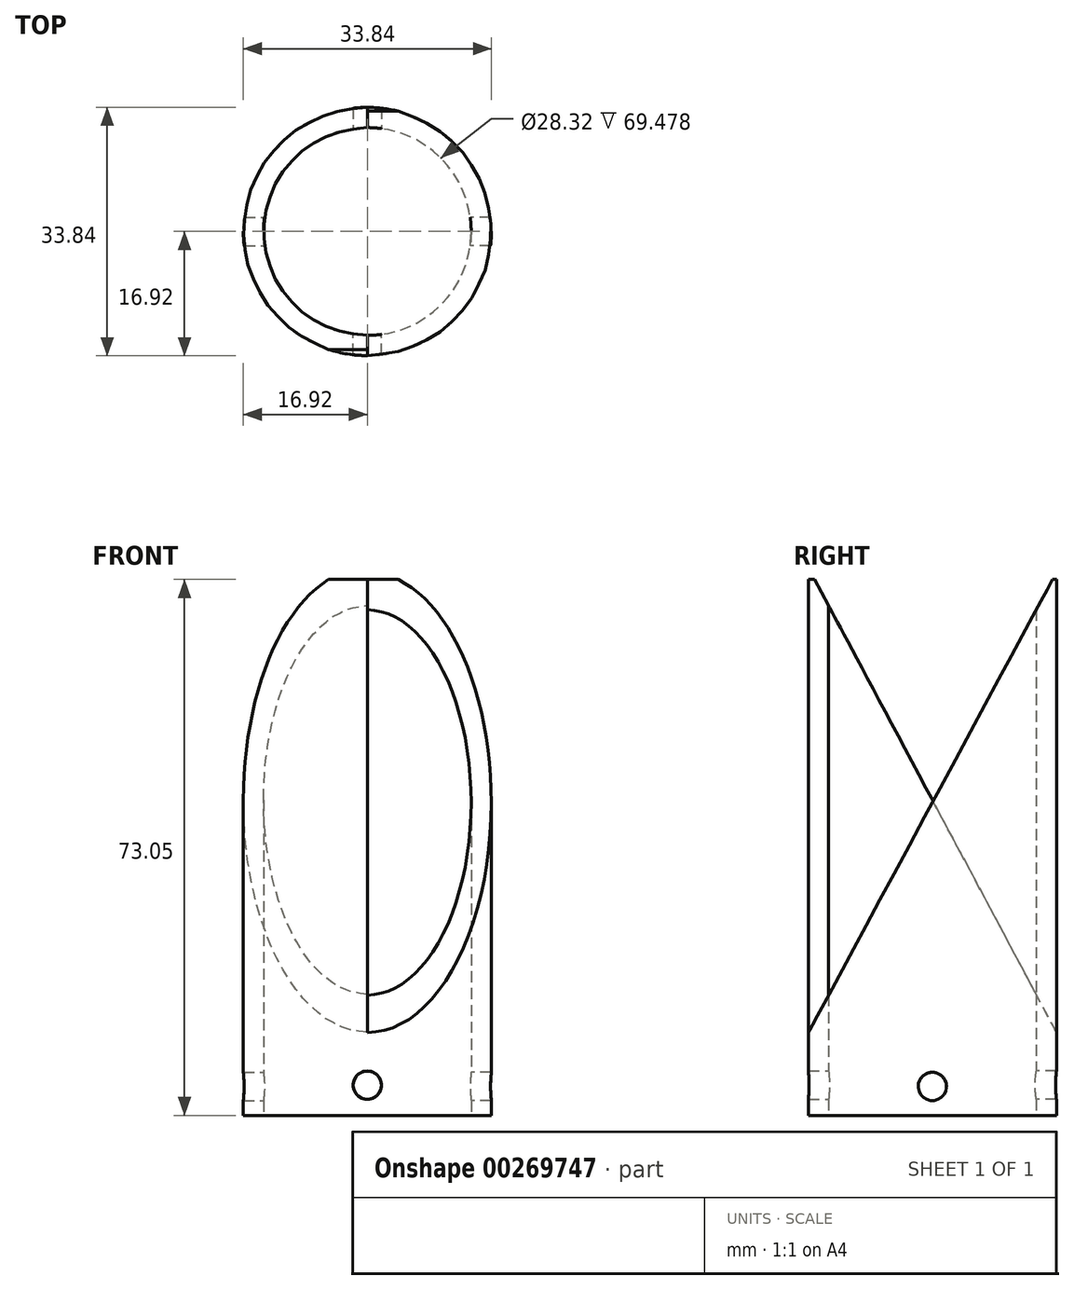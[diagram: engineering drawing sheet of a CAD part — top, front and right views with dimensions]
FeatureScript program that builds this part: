
annotation { "Feature Type Name" : "Feature", "Feature Type Description" : "" }
export const myFeature = defineFeature(function(context is Context, id is Id, definition is map)
    precondition{}
    {
        {
            var Q0;
            Q0=qCreatedBy(makeId("Top.planeOp"),FACE);
            var sketch = newSketch(context, id + "F0", { "sketchPlane" : qUnion([Q0])});
            skCircle(sketch, "E0", {"center": v(0, 0) * mm, "radius": 16.92 * mm});
            skCircle(sketch, "E1", {"center": v(0, 0) * mm, "radius": 14.16 * mm});
            skSolve(sketch);
        }
        {
            var Q0;
            Q0 = qSketchRegion(id + "F0", true);
            extrude(context, id + "F1", {"entities" : qUnion([Q0]), "depth" : 73.05 * mm});
        }
        {
            var Q0;
            Q0=qCreatedBy(makeId("Right.planeOp"),FACE);
            var sketch = newSketch(context, id + "F2", { "sketchPlane" : qUnion([Q0])});
            skLineSegment(sketch, "E2", {"start": v(-18.92, 7.55) * mm, "end": v(19.26, 78.39) * mm});
            skLineSegment(sketch, "E3", {"start": v(19.26, 78.39) * mm, "end": v(-18.28, 78.39) * mm});
            skLineSegment(sketch, "E4", {"start": v(-18.28, 78.39) * mm, "end": v(-18.92, 7.55) * mm});
            skSolve(sketch);
        }
        {
            var Q0;
            Q0 = qSketchRegion(id + "F2", true);
            extrude(context, id + "F3", {"entities" : qUnion([Q0]), "operationType" : NewBodyOperationType.REMOVE, "depth" : 58.42 * mm});
        }
        {
            var Q0;
            Q0=qCreatedBy(makeId("Right.planeOp"),FACE);
            var sketch = newSketch(context, id + "F4", { "sketchPlane" : qUnion([Q0])});
            skLineSegment(sketch, "E5", {"start": v(18.2, 8.96) * mm, "end": v(-19.36, 79.2) * mm});
            skLineSegment(sketch, "E6", {"start": v(-19.36, 79.2) * mm, "end": v(23.54, 79.2) * mm});
            skLineSegment(sketch, "E7", {"start": v(23.54, 79.2) * mm, "end": v(18.2, 8.96) * mm});
            skSolve(sketch);
        }
        {
            var Q0;
            Q0 = qSketchRegion(id + "F4", true);
            extrude(context, id + "F5", {"entities" : qUnion([Q0]), "operationType" : NewBodyOperationType.REMOVE, "oppositeDirection" : true, "depth" : 25.4 * mm});
        }
        {
            var Q0;
            Q0=qCreatedBy(makeId("Right.planeOp"),FACE);
            var sketch = newSketch(context, id + "F6", { "sketchPlane" : qUnion([Q0])});
            skCircle(sketch, "E8", {"center": v(0, 3.94) * mm, "radius": 1.93 * mm});
            skSolve(sketch);
        }
        {
            var Q0;
            Q0 = qSketchRegion(id + "F6", true);
            extrude(context, id + "F7", {"entities" : qUnion([Q0]), "operationType" : NewBodyOperationType.REMOVE, "oppositeDirection" : true, "depth" : 25.4 * mm});
        }
        {
            var Q0;
            Q0=qCreatedBy(makeId("Right.planeOp"),FACE);
            var sketch = newSketch(context, id + "F8", { "sketchPlane" : qUnion([Q0])});
            skCircle(sketch, "E9", {"center": v(0, 3.94) * mm, "radius": 1.93 * mm});
            skSolve(sketch);
        }
        {
            var Q0;
            Q0 = qSketchRegion(id + "F8", true);
            extrude(context, id + "F9", {"entities" : qUnion([Q0]), "operationType" : NewBodyOperationType.REMOVE, "depth" : 35.81 * mm});
        }
        {
            var Q0;
            Q0=qCreatedBy(makeId("Front.planeOp"),FACE);
            var sketch = newSketch(context, id + "F10", { "sketchPlane" : qUnion([Q0])});
            skCircle(sketch, "E10", {"center": v(0, 4.13) * mm, "radius": 1.93 * mm});
            skSolve(sketch);
        }
        {
            var Q0;
            Q0 = qSketchRegion(id + "F10", true);
            extrude(context, id + "F11", {"entities" : qUnion([Q0]), "operationType" : NewBodyOperationType.REMOVE, "oppositeDirection" : true, "depth" : 25.4 * mm});
        }
        {
            var Q0;
            Q0=qCreatedBy(makeId("Front.planeOp"),FACE);
            var sketch = newSketch(context, id + "F12", { "sketchPlane" : qUnion([Q0])});
            skCircle(sketch, "E11", {"center": v(0, 4.12) * mm, "radius": 1.93 * mm});
            skSolve(sketch);
        }
        {
            var Q0;
            Q0 = qSketchRegion(id + "F12", true);
            extrude(context, id + "F13", {"entities" : qUnion([Q0]), "operationType" : NewBodyOperationType.REMOVE, "depth" : 44.2 * mm});
        }
    });
